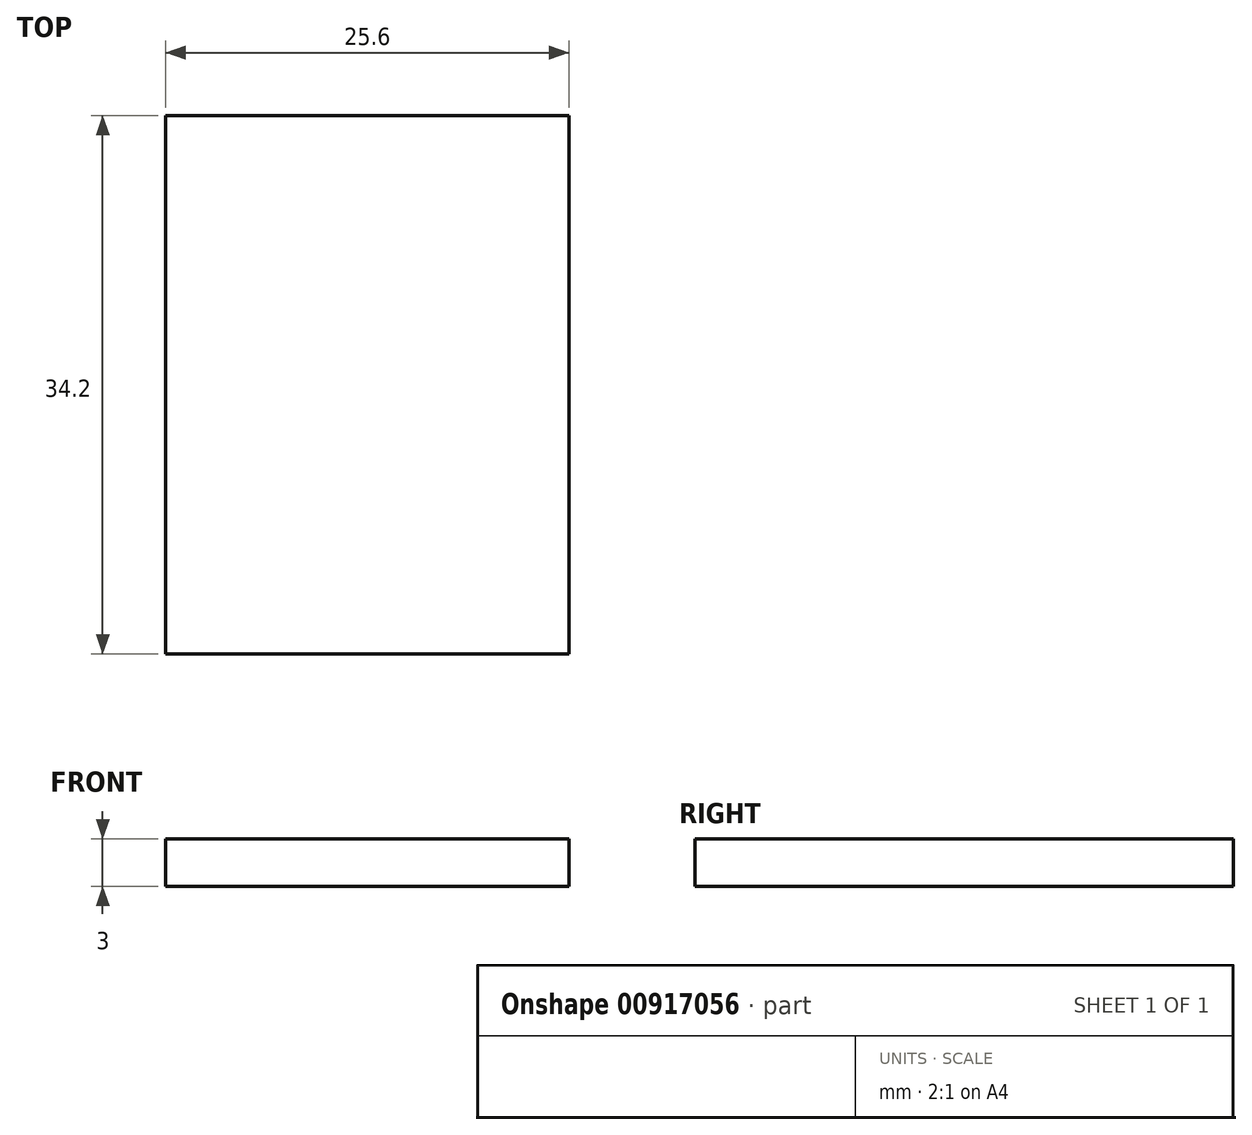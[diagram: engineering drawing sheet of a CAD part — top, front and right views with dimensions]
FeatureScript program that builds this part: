
annotation { "Feature Type Name" : "Feature", "Feature Type Description" : "" }
export const myFeature = defineFeature(function(context is Context, id is Id, definition is map)
    precondition{}
    {
        {
            var Q0;
            Q0=qCreatedBy(makeId("Top.planeOp"),FACE);
            var sketch = newSketch(context, id + "F0", { "sketchPlane" : qUnion([Q0])});
            skLineSegment(sketch, "E0.bottom", {"start": v(12.8, 17.1) * mm, "end": v(-12.8, 17.1) * mm});
            skLineSegment(sketch, "E0.top", {"start": v(12.8, -17.1) * mm, "end": v(-12.8, -17.1) * mm});
            skLineSegment(sketch, "E0.left", {"start": v(12.8, 17.1) * mm, "end": v(12.8, -17.1) * mm});
            skLineSegment(sketch, "E0.right", {"start": v(-12.8, 17.1) * mm, "end": v(-12.8, -17.1) * mm});
            skPoint(sketch, "E0.middle", {"position": v(0, 0) * mm});
            skSolve(sketch);
        }
        {
            var Q0;
            Q0=makeQuery(id+"F0.imprint","IMPRINT",FACE,{"disambiguationData":[TD([[makeQuery(id+"F0.imprint","IMPRINT",EDGE,{"derivedFrom":sQuery(id+"F0.wireOp",EDGE,"E0.bottom")}),1.0]])]});
            extrude(context, id + "F1", {"entities" : qUnion([Q0]), "endBound" : BoundingType.SYMMETRIC, "depth" : 3 * mm, "offsetDistance" : 25 * mm});
        }
    });
